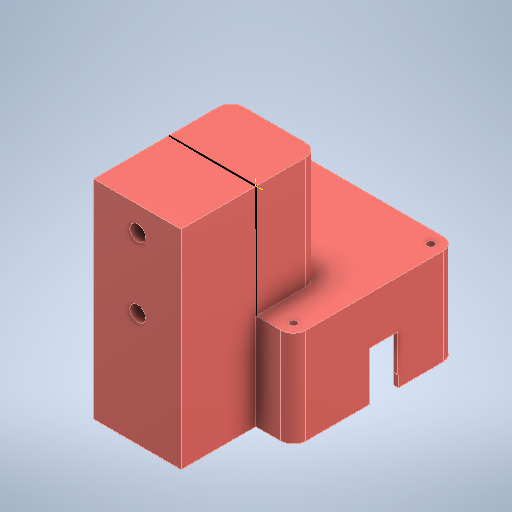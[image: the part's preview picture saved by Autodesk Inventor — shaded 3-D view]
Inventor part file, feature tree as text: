
AUTODESK INVENTOR PART (.ipt)
format: ipt  version: 2025.2 (Build 292293000, 293)  size: 932,864 bytes
history: native  units: in
note: dims shown in document units (in); Inventor stores cm internally (conversion verified against a paired STEP export)
features: move_body x42, sketch x39, extrude x35, fillet x11, direct_edit x9, other x5, projected_geometry x1
ambient origin geometry x8: Origin, YZ Plane, XZ Plane, XY Plane, X Axis, Y Axis, Z Axis, Center Point
bodies: Solid1 (feature_tree)
feature tree (142):
  direct_edit  "Direct Edit1"
  extrude  "Extrusion1"  Depth=0.4331in
  fillet  "Fillet1"  Radius=0.3543in
  fillet  "Fillet2"  Radius=0.4331in
  extrude  "Extrusion2"  Depth=0.1575in
  extrude  "Extrusion3"  Depth=0.1575in
  direct_edit  "Direct Edit2"
  extrude  "Extrusion4"  Depth=0.1667in
  extrude  "Extrusion5"  Depth=0.1575in TaperAngle=0.0deg
  extrude  "Extrusion6"  Depth=0.1575in TaperAngle=0.0deg
  extrude  "Extrusion7"  Depth=1.0812in TaperAngle=0.0deg
  extrude  "Extrusion8"  Depth=0.2938in TaperAngle=0.0deg
  extrude  "Extrusion9"  Depth=0.0787in TaperAngle=0.0deg
  extrude  "Extrusion10"  Depth=0.0787in TaperAngle=0.0deg
  extrude  "Extrusion11"  Depth=0.0787in TaperAngle=0.0deg
  extrude  "Extrusion12"  Depth=0.0787in TaperAngle=0.0deg
  extrude  "Extrusion13"  Depth=2.1654in
  extrude  "Extrusion14"  Depth=0.3937in
  extrude  "Extrusion15"  Depth=1.7717in
  extrude  "Extrusion16"  Depth=0.3937in
  extrude  "Extrusion17"  Depth=0.2756in
  extrude  "Extrusion18"  Depth=0.4724in
  fillet  "Fillet3"  Radius=0.4724in
  fillet  "Fillet4"  Radius=0.2165in
  fillet  "Fillet5"  Radius=0.1969in
  fillet  "Fillet6"  Radius=0.1969in
  fillet  "Fillet7"  Radius=0.1969in
  direct_edit  "Direct Edit3"
  direct_edit  "Direct Edit4"
  fillet  "Fillet8"  Radius=0.1969in
  fillet  "Fillet9"  Radius=0.1969in
  fillet  "Fillet10"  Radius=0.0787in
  fillet  "Fillet11"  Radius=0.0787in
  direct_edit  "Direct Edit5"
  direct_edit  "Direct Edit9"
  extrude  "Extrusion23"  Depth=0.0787in
  extrude  "Extrusion24"  Depth=0.3125in TaperAngle=0.0deg
  extrude  "Extrusion25"  Depth=0.1969in TaperAngle=0.0deg
  extrude  "Extrusion26"  Depth=0.1969in TaperAngle=0.0deg
  sketch  "Sketch28"  dims[d90=0.0in d91=0.0in d92=0.1969in]
  sketch  "Sketch29"  dims[d93=0.0in d94=0.0in d95=0.0625in d96=0.0787in d97=0.0787in]
  extrude  "Extrusion27"  TaperAngle=0.0deg  [1 undecoded]
  extrude  "Extrusion28"  Depth=0.315in TaperAngle=0.0deg
  sketch  "Sketch31"  dims[d100=0.0in d101=0.0in d102=0.315in d103=0.0in d104=0.0in d105=0.3125in]
  extrude  "Extrusion29"  TaperAngle=0.0deg  [1 undecoded]
  extrude  "Extrusion30"  TaperAngle=0.0deg  [1 undecoded]
  extrude  "Extrusion31"  TaperAngle=0.0deg  [1 undecoded]
  sketch  "Sketch35"  dims[d124=0.0in d125=0.0in d126=-0.0079in d127=0.0in d128=0.0in d129=0.315in]
  extrude  "Extrusion32"  TaperAngle=0.0deg  [1 undecoded]
  extrude  "Extrusion33"  TaperAngle=0.0deg  [1 undecoded]
  extrude  "Extrusion34"  TaperAngle=0.0deg  [1 undecoded]
  extrude  "Extrusion35"  TaperAngle=0.0deg  [1 undecoded]
  direct_edit  "Direct Edit6"
  direct_edit  "Direct Edit7"
  direct_edit  "Direct Edit8"
  extrude  "Extrusion19"  TaperAngle=0.0deg  [1 undecoded]
  extrude  "Extrusion20"  Depth=1.9685in TaperAngle=0.0deg
  extrude  "Extrusion21"  Depth=1.9685in TaperAngle=0.0deg
  extrude  "Extrusion22"  Depth=1.9685in TaperAngle=0.0deg
  sketch  "Sketch23"  dims[d75=0.0in d76=0.0in d77=0.1969in]
  sketch  "Sketch1"  dims[d0=0.3543in d1=0.4331in d2=0.3543in d3=0.4331in]
  sketch  "Sketch2"  dims[d4=0.1575in d5=0.0in d6=0.1575in]
  sketch  "Sketch3"  dims[d7=0.1575in d8=1.0885in]
  projected_geometry  "Projected Loop1"
  sketch  "Sketch4"  dims[d9=0.1667in d10=0.1667in]
  sketch  "Sketch5"  dims[d11=1.0866in d12=0.1575in d13=0.0in]
  sketch  "Sketch6"  dims[d14=0.1667in d15=0.1575in d16=0.0in]
  sketch  "Sketch7"  dims[d17=0.8563in d18=0.0in d19=1.0812in d20=0.0in]
  sketch  "Sketch8"  dims[d21=0.3312in d22=0.0in d23=0.2938in d24=0.0in]
  sketch  "Sketch9"  dims[d25=0.0787in d26=0.0in d27=0.0787in d28=0.0in]
  sketch  "Sketch10"  dims[d29=0.0787in d30=0.0in d31=0.0787in d32=0.0in]
  sketch  "Sketch11"  dims[d33=0.0787in d34=0.0in d35=0.0787in d36=0.0in]
  sketch  "Sketch12"  dims[d37=0.0787in d38=0.0in d39=0.0787in d40=0.0in]
  sketch  "Sketch13"  dims[d41=1.378in d42=2.1654in]
  sketch  "Sketch14"  dims[d43=0.3937in d44=0.3937in]
  sketch  "Sketch15"  dims[d45=1.7717in d46=0.0in d47=0.2441in]
  sketch  "Sketch16"  dims[d48=0.689in d49=0.3937in]
  sketch  "Sketch17"  dims[d50=0.2441in d51=0.2756in]
  sketch  "Sketch18"  dims[d52=0.9843in d53=0.0in d54=0.4724in d55=0.4724in d56=0.2165in d57=0.0in d58=0.1969in d59=0.1969in d60=0.1969in d61=0.1969in d62=0.1969in]
  sketch  "Sketch19"  dims[d63=0.0in d64=0.0in d65=0.1969in]
  sketch  "Sketch20"  dims[d66=0.0in d67=0.0in d68=0.1969in]
  sketch  "Sketch21"  dims[d69=0.0in d70=0.0in d71=0.1969in]
  sketch  "Sketch22"  dims[d72=0.0in d73=0.0in d74=0.1969in]
  sketch  "Sketch24"  dims[d78=0.0in d79=0.0in d80=0.1969in]
  sketch  "Sketch25"  dims[d81=0.0in d82=0.0in d83=0.1969in]
  sketch  "Sketch26"  dims[d84=0.0in d85=0.0in d86=0.1969in]
  sketch  "Sketch27"  dims[d87=0.0in d88=0.0in d89=0.1969in]
  sketch  "Sketch30"  dims[d98=0.0787in d99=0.0787in]
  sketch  "Sketch32"  dims[d106=0.0in d107=0.0in d108=0.0024in d109=0.0in d110=0.0in d111=0.1969in]
  sketch  "Sketch33"  dims[d112=0.0in d113=0.0in d114=0.1969in d115=0.0in d116=0.0in d117=0.0272in]
  sketch  "Sketch34"  dims[d118=0.0in d119=0.0in d120=0.0272in d121=0.0in d122=0.0in d123=-0.0079in]
  sketch  "Sketch36"  dims[d130=0.0in d131=0.0in d132=0.1969in d133=0.0in d134=0.0in d135=-0.4724in]
  sketch  "Sketch37"  dims[d136=0.0689in d137=0.0in d138=0.0in d139=0.0in d140=-0.1181in]
  sketch  "Sketch38"  dims[d141=0.0in d142=0.0in d143=0.0276in d144=0.0in d145=0.0in d146=-0.0197in]
  sketch  "Sketch39"  dims[d147=0.0in d148=0.0in d149=-0.0197in d150=0.0in d151=0.0in d152=-0.0197in d153=0.0in d154=0.0in d155=-0.0197in d156=0.0in d157=0.0in d158=-0.0197in d159=0.0in d160=0.0in d161=-0.0197in d162=0.0in d163=0.0in d164=-0.0197in d165=0.5064in d166=0.0in d167=0.5064in d168=0.0in d169=0.5064in d170=0.0in d171=0.0in d172=0.0in d173=0.2165in d174=0.0in d175=0.0in d176=0.2165in d177=0.0in d178=0.0in d179=0.2165in d180=0.0in d181=0.0in d182=-0.2165in d183=0.0in d184=0.0in d185=-0.2165in d186=0.0in d187=0.0in d188=0.2165in d189=0.0in d190=0.0in d191=-0.4724in d192=0.5187in d193=0.0in d194=0.0in d195=0.0in d196=-0.0197in d197=0.0in d198=0.0in d199=0.0787in d200=0.5187in d201=0.0in d202=0.3937in d203=0.0in d204=0.4562in d205=0.0in d206=2.2721in d207=0.0in d208=0.3937in d209=0.0in d210=1.1811in d211=0.0in d212=0.3937in d213=0.0in d214=0.3937in d215=0.0in d216=0.3937in d217=0.0in d218=0.4724in d219=0.5118in d220=0.0in d221=0.0in d222=-0.0787in d223=0.1378in d224=0.0551in d225=0.1181in d226=0.0in d227=0.0in d228=0.1378in d229=0.0551in d230=0.1181in d231=0.0in d232=0.0in d233=1.5118in d234=0.0in d235=0.5512in d236=0.3937in d237=0.0in d238=1.9685in]
  other  "Com_Top_A"
  other  "Delete1"
  other  "Delete2"
  other  "Delete3"
  other  "Delete4"
  move_body  "Move1"
  move_body  "Move2"
  move_body  "Move3"
  move_body  "Move4"
  move_body  "Move5"
  move_body  "Move6"
  move_body  "Move7"
  move_body  "Move8"
  move_body  "Move9"
  move_body  "Move10"
  move_body  "Move11"
  move_body  "Move12"
  move_body  "Move13"
  move_body  "Move14"
  move_body  "Move15"
  move_body  "Move16"
  move_body  "Move17"
  move_body  "Move18"
  move_body  "Move19"
  move_body  "Move20"
  move_body  "Move21"
  move_body  "Move22"
  move_body  "Move23"
  move_body  "Move24"
  move_body  "Move25"
  move_body  "Move26"
  move_body  "Move27"
  move_body  "Move28"
  move_body  "Move29"
  move_body  "Move30"
  move_body  "Move31"
  move_body  "Move32"
  move_body  "Move33"
  move_body  "Move34"
  move_body  "Move35"
  move_body  "Move36"
  move_body  "Move37"
  move_body  "Move38"
  move_body  "Move39"
  move_body  "Move40"
  move_body  "Move41"
  move_body  "Move42"
note: 9 required parameter values undecoded (feature->parameter linkage not recoverable at this tier; creation-order binding heuristic only, values carry confidence <= 0.55)
